# Revit family: Toilet-Elongated-American_Standard-Rapidway-3445_Series
name_source: partatom
category: Plumbing Fixtures
revit_build: Autodesk Revit 2014 (Build: 20130308_1515(x64)
units: mm (PartAtom-declared; Revit-internal decimal feet)

## types (2) — shared parameters
ADA Compliant = Yes
Assembly Code = D2010110
Bowl Shape = Elongated
CW Connection = Yes
CWFU = 10
Cold Water Connection Diameter = 1"
Cold Water Connection Radius = 1/2"
Cold Water Connection Width = 4 3/4"
Default Elevation = 15 1/2"
Finish = Vitreous China-American Standard-020-White
Flush Rate = 1.6 gpf (6.0 Lpf)
HW Connection = No
Height = 15 1/2"
Installation Type = Wall Mounted
Length = 25"
Manufacturer = American Standard
Material = Vitreous China-American Standard-020-White
Price = Prices may vary. Please consult Manufacturer Representative for most up-to-date price list.
Product Documentation Link = https://www.americanstandard-us.com
Product Page URL = https://www.americanstandard-us.com
URL = http://www.americanstandard-us.com
Vent Connection = No
WFU = 10
Waste Connection = Yes
Waste Connection Diameter = 2 1/8"
Waste Connection Radius = 1 1/16"
Width = 14"
zero-valued in all types: HWFU

## per-type parameters (varying)
| type | Back Spud | Back Spud Description | Back Spud Supply Radius | Cold Water Connection Height | Description | Top Spud | Top Spud Description | Top Spud Supply Radius | Waste Connection Height |
| 3445J.101.020 | No |  | 0" | 25 7/8" | Rapidway Top Spud Elongated Toilet | Yes | 1'' I.P.S CW Inlet | 1/2" | 12 1/4" |
| 3445L.101.020 | Yes | 1'' I.P.S CW Inlet | 1/2" | 14" | Rapidway Back Spud Elongated Toilet | No |  | 0" | 5 1/4" |

note: column(s) folded — value = type name in every type: Model

## geometry (parser evidence)
native form markers: Sweep x1
no freeform markers — native parametric forms only
